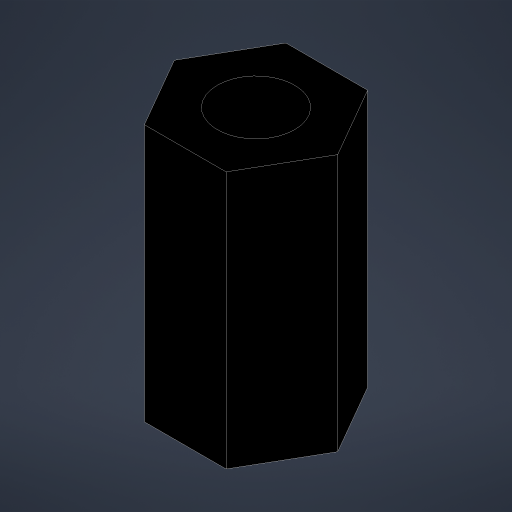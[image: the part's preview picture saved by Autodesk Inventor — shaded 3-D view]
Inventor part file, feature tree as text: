
AUTODESK INVENTOR PART (.ipt)
format: ipt  version: 2025 (Build 290162010, 162A)  size: 158,720 bytes
history: native  units: mm
features: extrude x1, sketch x1
ambient origin geometry x8: Origin, YZ Plane, XZ Plane, XY Plane, X Axis, Y Axis, Z Axis, Center Point
bodies: Solid1 (feature_tree)
feature tree (2):
  extrude  "Extrusion1"  Depth=10.0mm
  sketch  "Sketch1"  dims[d0=5.5mm d1=3.0mm d2=10.0mm d3=0.0mm d4=0.5mm d5=0.872665mm]
